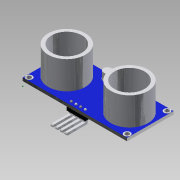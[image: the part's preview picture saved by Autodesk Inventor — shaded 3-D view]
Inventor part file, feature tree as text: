
AUTODESK INVENTOR PART (.ipt)
format: ipt  version: 2015 (Build 190159000, 159)  size: 408,064 bytes
history: native  units: mm
features: sketch x21, projected_geometry x16, extrude x15, revolve x4
ambient origin geometry x8: Origin, YZ Plane, XZ Plane, XY Plane, X Axis, Y Axis, Z Axis, Center Point
bodies: Solid1 (feature_tree)
feature tree (56):
  extrude  "Extrusion1"  Depth=20.0mm
  extrude  "Extrusion2"  Depth=7.0mm TaperAngle=0.0deg
  extrude  "Extrusion3"  Depth=7.0mm TaperAngle=0.0deg
  extrude  "Extrusion4"  Depth=13.0mm
  extrude  "Extrusion5"  Depth=5.0mm TaperAngle=0.0deg
  extrude  "Extrusion6"  Depth=0.2mm TaperAngle=0.0deg
  extrude  "Extrusion7"  Depth=3.0mm
  extrude  "Extrusion8"  Depth=2.0mm
  extrude  "Extrusion9"  Depth=0.1mm TaperAngle=0.0deg
  extrude  "Extrusion10"  Depth=0.1mm TaperAngle=0.0deg
  extrude  "Extrusion11"  TaperAngle=90.0deg  [1 undecoded]
  revolve  "Revolution1"  Angle=180.0deg
  revolve  "Revolution2"  [1 undecoded]
  revolve  "Revolution3"  [1 undecoded]
  revolve  "Revolution4"  [1 undecoded]
  extrude  "Extrusion12"  Depth=8.0mm TaperAngle=0.0deg
  sketch  "Sketch17"  dims[d68=0.5mm d69=0.5mm]
  sketch  "Sketch18"  dims[d70=80.0mm d71=0.0mm]
  extrude  "Extrusion13"  Depth=0.5mm
  extrude  "Extrusion14"  [1 undecoded]
  extrude  "Extrusion15"  [1 undecoded]
  sketch  "Sketch1"  dims[d0=45.0mm d1=20.0mm]
  sketch  "Sketch2"  dims[d2=1.3mm d3=0.0mm d6=7.0mm d7=0.0mm]
  sketch  "Sketch3"  dims[d13=7.0mm d14=0.0mm d19=7.0mm d20=0.0mm]
  sketch  "Sketch4"  dims[d21=13.0mm d22=13.0mm]
  sketch  "Sketch5"  dims[d23=10.0mm d24=0.0mm d25=5.0mm d26=0.0mm]
  projected_geometry  "Projected Loop1"
  projected_geometry  "Projected Loop2"
  sketch  "Sketch6"  dims[d27=1.0mm d28=0.0mm d36=0.2mm d37=0.0mm]
  projected_geometry  "Projected Loop3"
  projected_geometry  "Projected Loop4"
  sketch  "Sketch7"  dims[d42=3.0mm d43=0.0mm d44=2.7mm]
  projected_geometry  "Projected Loop5"
  sketch  "Sketch8"  dims[d45=2.7mm d46=2.0mm]
  projected_geometry  "Projected Loop6"
  sketch  "Sketch9"  dims[d47=2.7mm d48=0.1mm d49=0.0mm]
  projected_geometry  "Projected Loop7"
  sketch  "Sketch10"  dims[d50=2.7mm d51=0.1mm d52=0.0mm]
  projected_geometry  "Projected Loop8"
  sketch  "Sketch11"  dims[d53=90.0deg d54=90.0deg]
  sketch  "Sketch12"  dims[d55=180.0deg d56=180.0deg]
  projected_geometry  "Projected Loop9"
  sketch  "Sketch13"  dims[d57=180.0deg d58=2.0mm]
  projected_geometry  "Projected Loop10"
  sketch  "Sketch14"  dims[d59=2.0mm d60=2.0mm]
  sketch  "Sketch15"  dims[d61=2.0mm d62=2.0mm d63=0.0mm]
  sketch  "Sketch16"  dims[d64=2.0mm d65=0.0mm d66=8.0mm d67=0.0mm]
  projected_geometry  "Projected Loop11"
  sketch  "Sketch19"
  projected_geometry  "Projected Loop12"
  sketch  "Sketch20"
  projected_geometry  "Projected Loop13"
  projected_geometry  "Projected Loop14"
  projected_geometry  "Projected Loop15"
  sketch  "Sketch21"
  projected_geometry  "Projected Loop16"
note: 6 required parameter values undecoded (feature->parameter linkage not recoverable at this tier; creation-order binding heuristic only, values carry confidence <= 0.55)